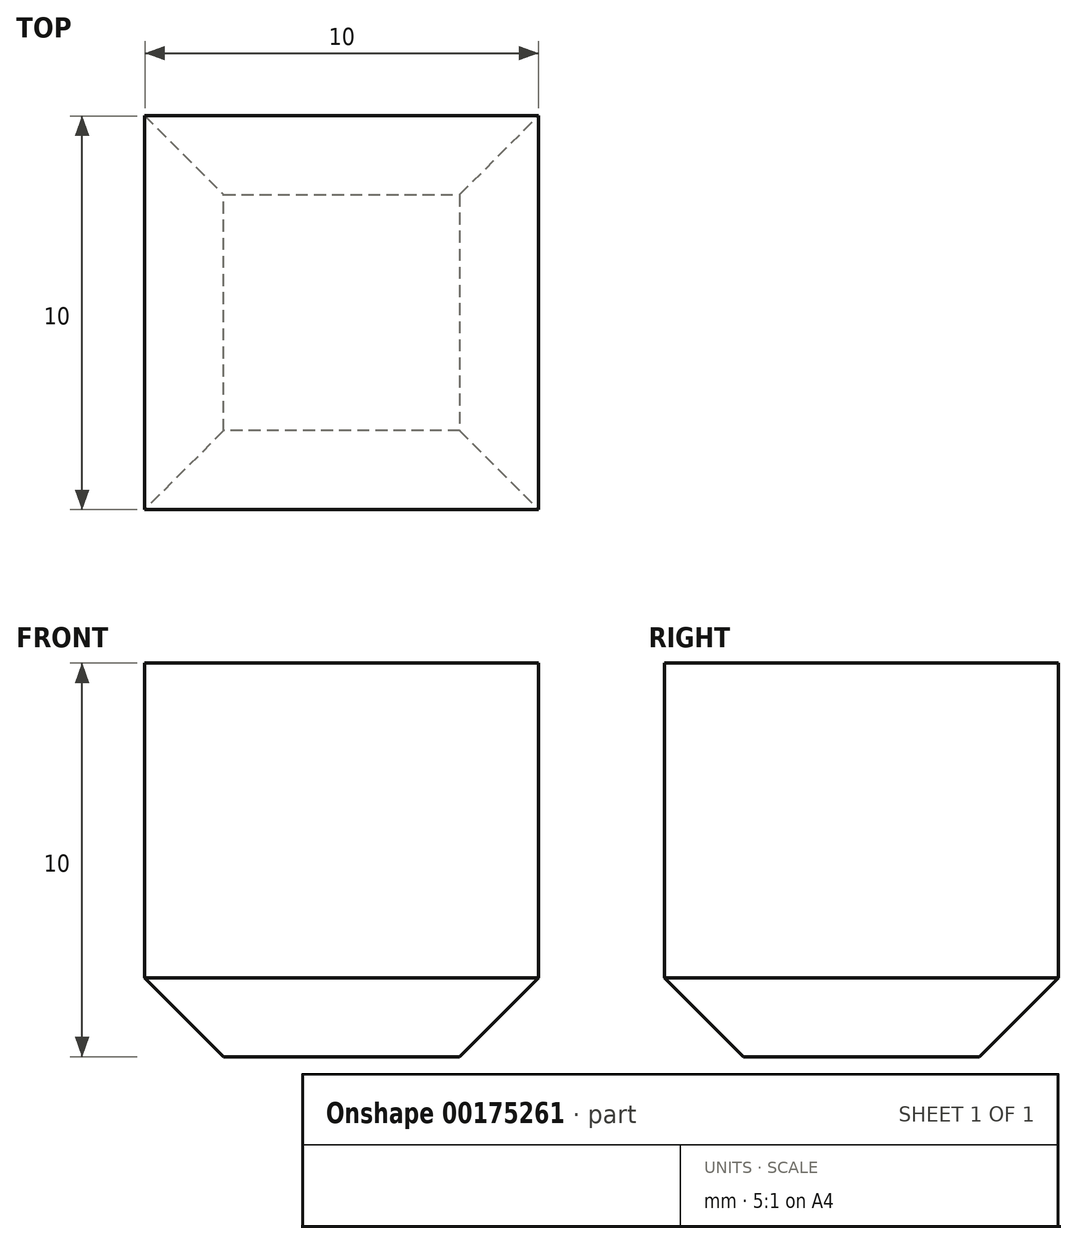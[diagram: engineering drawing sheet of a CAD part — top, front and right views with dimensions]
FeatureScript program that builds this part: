
annotation { "Feature Type Name" : "Feature", "Feature Type Description" : "" }
export const myFeature = defineFeature(function(context is Context, id is Id, definition is map)
    precondition{}
    {
        {
            var Q0;
            Q0=qCreatedBy(makeId("Top.planeOp"),FACE);
            var sketch = newSketch(context, id + "F0", { "sketchPlane" : qUnion([Q0])});
            skLineSegment(sketch, "E0.bottom", {"start": v(0.92, -1.69) * mm, "end": v(10.92, -1.69) * mm});
            skLineSegment(sketch, "E0.top", {"start": v(0.92, -11.69) * mm, "end": v(10.92, -11.69) * mm});
            skLineSegment(sketch, "E0.left", {"start": v(0.92, -1.69) * mm, "end": v(0.92, -11.69) * mm});
            skLineSegment(sketch, "E0.right", {"start": v(10.92, -1.69) * mm, "end": v(10.92, -11.69) * mm});
            skSolve(sketch);
        }
        {
            var Q0;
            Q0 = qSketchRegion(id + "F0", true);
            extrude(context, id + "F1", {"entities" : qUnion([Q0]), "depth" : 10 * mm});
        }
        {
            var Q0;
            Q0=makeQuery(id+"F1.opExtrude","CAP_EDGE",EDGE,{"disambiguationData":[OSD([sQuery(id+"F0.wireOp",EDGE,"E0.top")])],"isStart":true});
            var Q1;
            Q1=makeQuery(id+"F1.opExtrude","CAP_EDGE",EDGE,{"disambiguationData":[OSD([sQuery(id+"F0.wireOp",EDGE,"E0.left")])],"isStart":true});
            var Q2;
            Q2=makeQuery(id+"F1.opExtrude","CAP_EDGE",EDGE,{"disambiguationData":[OSD([sQuery(id+"F0.wireOp",EDGE,"E0.bottom")])],"isStart":true});
            var Q3;
            Q3=makeQuery(id+"F1.opExtrude","CAP_EDGE",EDGE,{"disambiguationData":[OSD([sQuery(id+"F0.wireOp",EDGE,"E0.right")])],"isStart":true});
            chamfer(context, id + "F2", {"entities" : qUnion([Q0, Q1, Q2, Q3]), "width" : 2 * mm, "tangentPropagation" : true});
        }
    });
